# Revit family: BC_Hitachi_Duct-MSP-RPI_LOD400
name_source: partatom
category: Mechanical Equipment
revit_build: Autodesk Revit 2018 (Build: 20170223_1515(x64)
units: mm (PartAtom-declared; Revit-internal decimal feet)

## family parameters
Always vertical = Yes
Cut with Voids When Loaded = No
OmniClass Number = 23.75.10.00
OmniClass Title = Transformation and Conversion of Energy
Part Type = Normal
Room Calculation Point = No
Round Connector Dimension = Use Diameter
Shared = No
Work Plane-Based = No

## types (7) — shared parameters
BC_MODEL_ID = 513159
BC_OBJECT_ID = 208597
BC_OBJECT_VERSION = #4
CALC_DGL = 16 mm
CALC_DLL = 6 mm  [stored 0.019685 ft]
CALC_HAI = 174 mm  [stored 0.570866 ft]
CALC_HAO = 162 mm  [stored 0.531496 ft]
Chute de Pression Evacuation = 0.0 Pa
Description = Duct MSP (RPI-FSRE/FSN6E)
Diamètre Evacuation = 32 mm  [stored 0.104987 ft]
Diamètre Gaz = 16 mm
Exhaust Pressure Drop = 0.0 Pa
Fréquence = 50 Hz
Hauteur de Reprise = 174 mm  [stored 0.570866 ft]
Hauteur de Soufflage = 162 mm  [stored 0.531496 ft]
Hauteur hors tout = 240 mm  [stored 0.787402 ft]
Manufacturer = Hitachi Air Conditioning Europe SAS
MasterFormat = 23 73 00
Model = Duct MSP (RPI-FSRE/FSN6E)
Nombres de Pôles  = 1
Omniclass = 23-33 25 00
Profondeur hors tout = 600 mm
Tension AC Min = 207 V
Tension AC max = 253 V
Tension Nominale = 230 V
Type de réfrigérant = R410A / R32
Uniformat = D3040

## per-type parameters (varying)
| type | BC_VARIANT_ID | CALC_LAI | CALC_LAO | CALC_Lt1 | CALC_Lt2 | Calibre d'Intensité | Capacité | Capacité de Chauffage Nominale | Capacité de Refroidissement Nominale | Courant DC Maximal | Courant Nominal | Courant d'usage | Diamètre Etat Liquide  | Débit Air Maximum | Largeur de Reprise | Largeur de Soufflage | Largeur hors tout | Niveau de pression acoustique max | Puissance AC Nominale | Puissance Acoustique Maximum | Puissance utile nominale |
| RPI-1.5FSRE | 507782 | 663 mm  [stored 2.1752 ft] | 524 mm  [stored 1.71916 ft] | 98 mm | 239 mm | 1 A | 4000 W | 4800 W | 4000 W | 2 A | 1 A | 1 A | 6 mm  [stored 0.019685 ft] | 233.3 L/s | 663 mm  [stored 2.1752 ft] | 524 mm  [stored 1.71916 ft] | 750 mm  [stored 2.46063 ft] | 32 | 150 W | 55 | 150 W |
| RPI-2.0FSRE | 507783 | 663 mm  [stored 2.1752 ft] | 524 mm  [stored 1.71916 ft] | 98 mm | 239 mm | 1 A | 5600 W | 6300 W | 5600 W | 2 A | 1 A | 1 A | 6 mm  [stored 0.019685 ft] | 233.3 L/s | 663 mm  [stored 2.1752 ft] | 524 mm  [stored 1.71916 ft] | 750 mm  [stored 2.46063 ft] | 32 | 150 W | 58 | 150 W |
| RPI-2.5FSRE | 507784 | 997 mm  [stored 3.271 ft] | 858 mm  [stored 2.81496 ft] | 508 mm  [stored 1.66667 ft] | 649 mm  [stored 2.12927 ft] | 2 A | 7100 W | 8500 W | 7100 W | 3 A | 2 A | 2 A | 10 mm  [stored 0.0328084 ft] | 333.3 L/s | 997 mm  [stored 3.271 ft] | 858 mm  [stored 2.81496 ft] | 1084 mm  [stored 3.55643 ft] | 34 | 210 W | 57 | 210 W |
| RPI-3.0FSRE | 507785 | 997 mm  [stored 3.271 ft] | 858 mm  [stored 2.81496 ft] | 508 mm  [stored 1.66667 ft] | 649 mm  [stored 2.12927 ft] | 2 A | 8000 W | 9000 W | 8000 W | 3 A | 2 A | 2 A | 10 mm  [stored 0.0328084 ft] | 358.3 L/s | 997 mm  [stored 3.271 ft] | 858 mm  [stored 2.81496 ft] | 1084 mm  [stored 3.55643 ft] | 35 | 220 W | 59 | 220 W |
| RPI-4.0FSRE | 507786 | 1387 mm  [stored 4.55052 ft] | 1248 mm  [stored 4.09449 ft] | 702 mm | 843 mm | 2 A | 11200 W | 12500 W | 11200 W | 3 A | 2 A | 2 A | 10 mm  [stored 0.0328084 ft] | 600.0 L/s | 1387 mm  [stored 4.55052 ft] | 1248 mm  [stored 4.09449 ft] | 1474 mm  [stored 4.83596 ft] | 39 | 230 W | 62 | 230 W |
| RPI-5.0FSRE | 507787 | 1387 mm  [stored 4.55052 ft] | 1248 mm  [stored 4.09449 ft] | 702 mm | 843 mm | 3 A | 14000 W | 16000 W | 14000 W | 4 A | 3 A | 3 A | 10 mm  [stored 0.0328084 ft] | 616.7 L/s | 1387 mm  [stored 4.55052 ft] | 1248 mm  [stored 4.09449 ft] | 1474 mm  [stored 4.83596 ft] | 40 | 290 W | 64 | 290 W |
| RPI-6.0FSRE | 507790 | 1387 mm  [stored 4.55052 ft] | 1248 mm  [stored 4.09449 ft] | 702 mm | 843 mm | 3 A | 16000 W | 18000 W | 16000 W | 4 A | 3 A | 3 A | 10 mm  [stored 0.0328084 ft] | 625.0 L/s | 1387 mm  [stored 4.55052 ft] | 1248 mm  [stored 4.09449 ft] | 1474 mm  [stored 4.83596 ft] | 40 | 310 W | 64 | 310 W |

note: column(s) folded — value = type name in every type: Référence, Type Comments

note: [stored X ft] marks values corroborated as IEEE doubles in the binary element streams (Revit-internal decimal feet)

## geometry (parser evidence)
native form markers: Blend x2
no freeform markers — native parametric forms only
